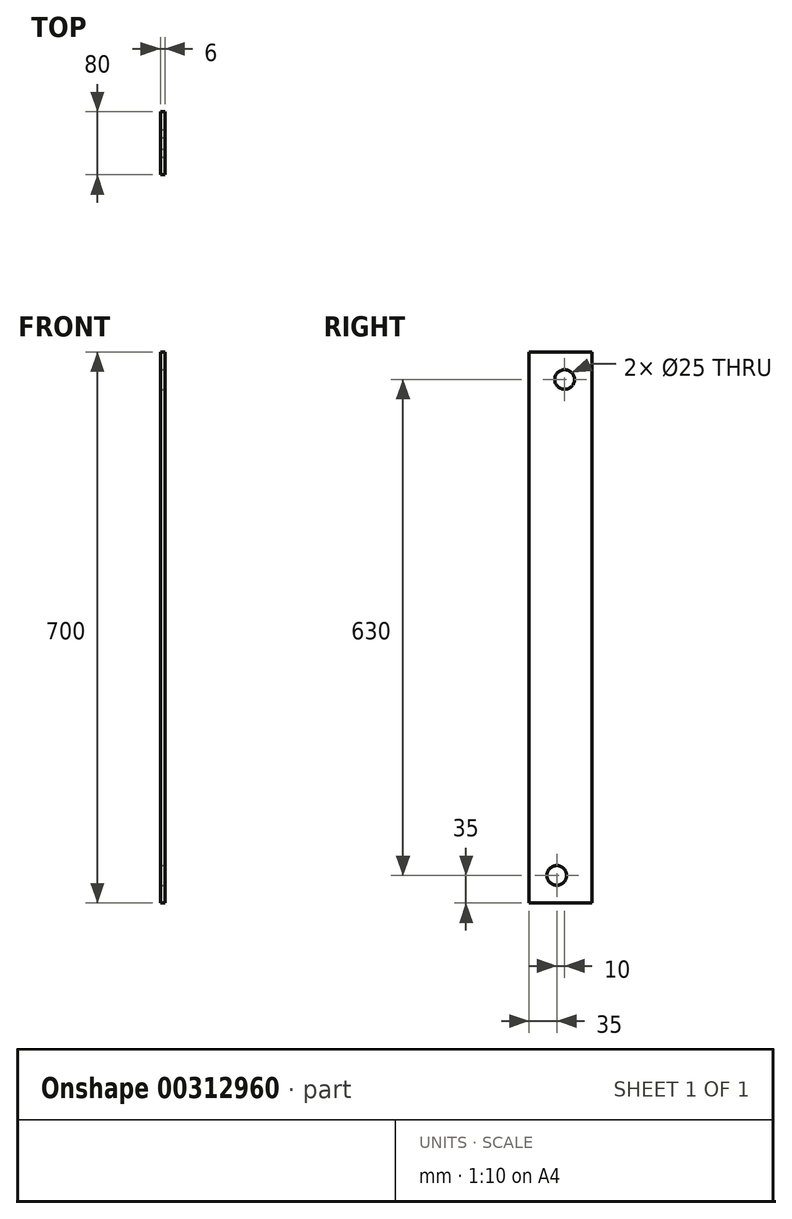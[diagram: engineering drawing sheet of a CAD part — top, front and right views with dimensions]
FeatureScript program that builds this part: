
annotation { "Feature Type Name" : "Feature", "Feature Type Description" : "" }
export const myFeature = defineFeature(function(context is Context, id is Id, definition is map)
    precondition{}
    {
        {
            var Q0;
            Q0=qCreatedBy(makeId("Right.planeOp"),FACE);
            var sketch = newSketch(context, id + "F0", { "sketchPlane" : qUnion([Q0])});
            skLineSegment(sketch, "E0.bottom", {"start": v(40, 350) * mm, "end": v(-40, 350) * mm});
            skLineSegment(sketch, "E0.top", {"start": v(40, -350) * mm, "end": v(-40, -350) * mm});
            skLineSegment(sketch, "E0.left", {"start": v(40, 350) * mm, "end": v(40, -350) * mm});
            skLineSegment(sketch, "E0.right", {"start": v(-40, 350) * mm, "end": v(-40, -350) * mm});
            skPoint(sketch, "E0.middle", {"position": v(0, 0) * mm});
            skSolve(sketch);
        }
        {
            var Q0;
            Q0 = qSketchRegion(id + "F0", true);
            extrude(context, id + "F1", {"entities" : qUnion([Q0]), "depth" : 6 * mm});
        }
        {
            var Q0;
            Q0=makeQuery(id+"F1.opExtrude","CAP_FACE",FACE,{"disambiguationData":[OSD([sQuery(id+"F0.wireOp",EDGE,"E0.bottom"),sQuery(id+"F0.wireOp",EDGE,"E0.top"),sQuery(id+"F0.wireOp",EDGE,"E0.left"),sQuery(id+"F0.wireOp",EDGE,"E0.right")])],"isStart":false});
            var sketch = newSketch(context, id + "F2", { "sketchPlane" : qUnion([Q0])});
            skCircle(sketch, "E1", {"center": v(5, 315) * mm, "radius": 12.5 * mm});
            skCircle(sketch, "E2", {"center": v(-5, -315) * mm, "radius": 12.5 * mm});
            skSolve(sketch);
        }
        {
            var Q0;
            Q0 = qSketchRegion(id + "F2", true);
            extrude(context, id + "F3", {"entities" : qUnion([Q0]), "operationType" : NewBodyOperationType.REMOVE, "oppositeDirection" : true, "depth" : 25 * mm});
        }
    });
